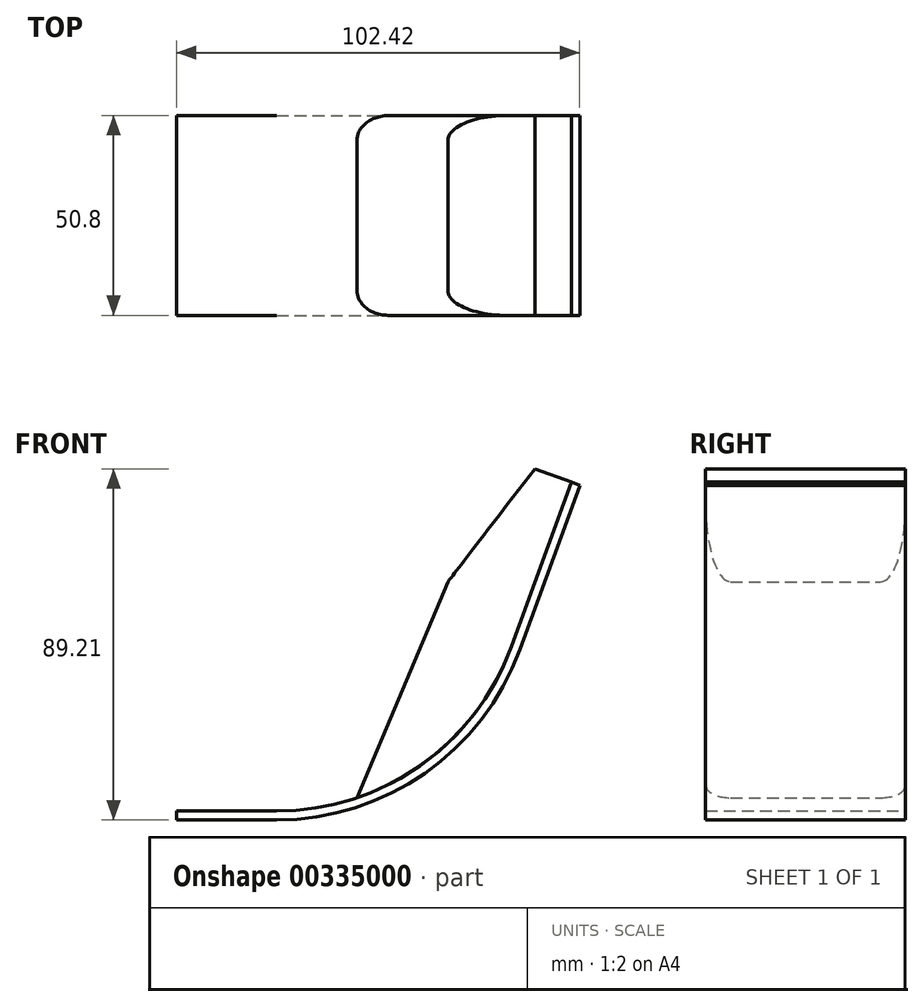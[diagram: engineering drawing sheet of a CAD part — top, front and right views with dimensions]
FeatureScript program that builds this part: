
annotation { "Feature Type Name" : "Feature", "Feature Type Description" : "" }
export const myFeature = defineFeature(function(context is Context, id is Id, definition is map)
    precondition{}
    {
        {
            var Q0;
            Q0=qCreatedBy(makeId("Front.planeOp"),FACE);
            var sketch = newSketch(context, id + "F0", { "sketchPlane" : qUnion([Q0])});
            skLineSegment(sketch, "E0", {"start": v(0, 0) * mm, "end": v(25.4, 0) * mm});
            skLineSegment(sketch, "E1", {"start": v(85.07, 41.78) * mm, "end": v(100.27, 83.55) * mm});
            skPoint(sketch, "E2.visualSharp", {"position": v(69.86, 0) * mm});
            skArc(sketch, "E2.filletArc", {"start": v(25.4, 0) * mm, "mid": v(61.82, 11.48) * mm, "end": v(85.07, 41.78) * mm});
            skLineSegment(sketch, "E3.0", {"start": v(87.22, 41) * mm, "end": v(102.42, 82.77) * mm});
            skArc(sketch, "E3.1", {"start": v(25.4, -2.29) * mm, "mid": v(63.13, 9.61) * mm, "end": v(87.22, 41) * mm});
            skLineSegment(sketch, "E3.2", {"start": v(0, -2.29) * mm, "end": v(25.4, -2.29) * mm});
            skLineSegment(sketch, "E4", {"start": v(0, 0) * mm, "end": v(0, -2.29) * mm});
            skLineSegment(sketch, "E5", {"start": v(100.27, 83.55) * mm, "end": v(102.42, 82.77) * mm});
            skSolve(sketch);
        }
        {
            var Q0;
            Q0 = qSketchRegion(id + "F0", true);
            extrude(context, id + "F1", {"entities" : qUnion([Q0]), "endBound" : BoundingType.SYMMETRIC, "depth" : 50.8 * mm});
        }
        {
            var Q0;
            Q0=qCreatedBy(makeId("Front.planeOp"),FACE);
            var sketch = newSketch(context, id + "F2", { "sketchPlane" : qUnion([Q0])});
            skLineSegment(sketch, "E6.0", {"start": v(85.07, 41.78) * mm, "end": v(100.27, 83.55) * mm});
            skArc(sketch, "E7.0", {"start": v(25.4, 0) * mm, "mid": v(61.82, 11.48) * mm, "end": v(85.07, 41.78) * mm});
            skLineSegment(sketch, "E8", {"start": v(100.27, 83.55) * mm, "end": v(91.02, 86.92) * mm});
            skLineSegment(sketch, "E9", {"start": v(91.02, 86.92) * mm, "end": v(68.93, 58.25) * mm});
            skLineSegment(sketch, "E10", {"start": v(68.93, 58.25) * mm, "end": v(45.84, 3.38) * mm});
            skSolve(sketch);
        }
        {
            var Q0;
            Q0 = qSketchRegion(id + "F2", true);
            extrude(context, id + "F3", {"entities" : qUnion([Q0]), "depth" : 25.4 * mm, "hasSecondDirection" : true, "secondDirectionOppositeDirection" : true, "secondDirectionDepth" : 25.4 * mm});
        }
        {
            var Q0;
            Q0=makeQuery(id+"F3.opExtrude","CAP_EDGE",EDGE,{"disambiguationData":[OSD([sQuery(id+"F2.wireOp",EDGE,"E10")])],"isStart":false});
            var Q1;
            Q1=makeQuery(id+"F3.opExtrude","CAP_EDGE",EDGE,{"disambiguationData":[OSD([sQuery(id+"F2.wireOp",EDGE,"E10")])],"isStart":true});
            fillet(context, id + "F4", {"entities" : qUnion([Q0, Q1]), "radius" : 6.35 * mm, "tangentPropagation" : true, "allowEdgeOverflow" : false});
        }
    });
